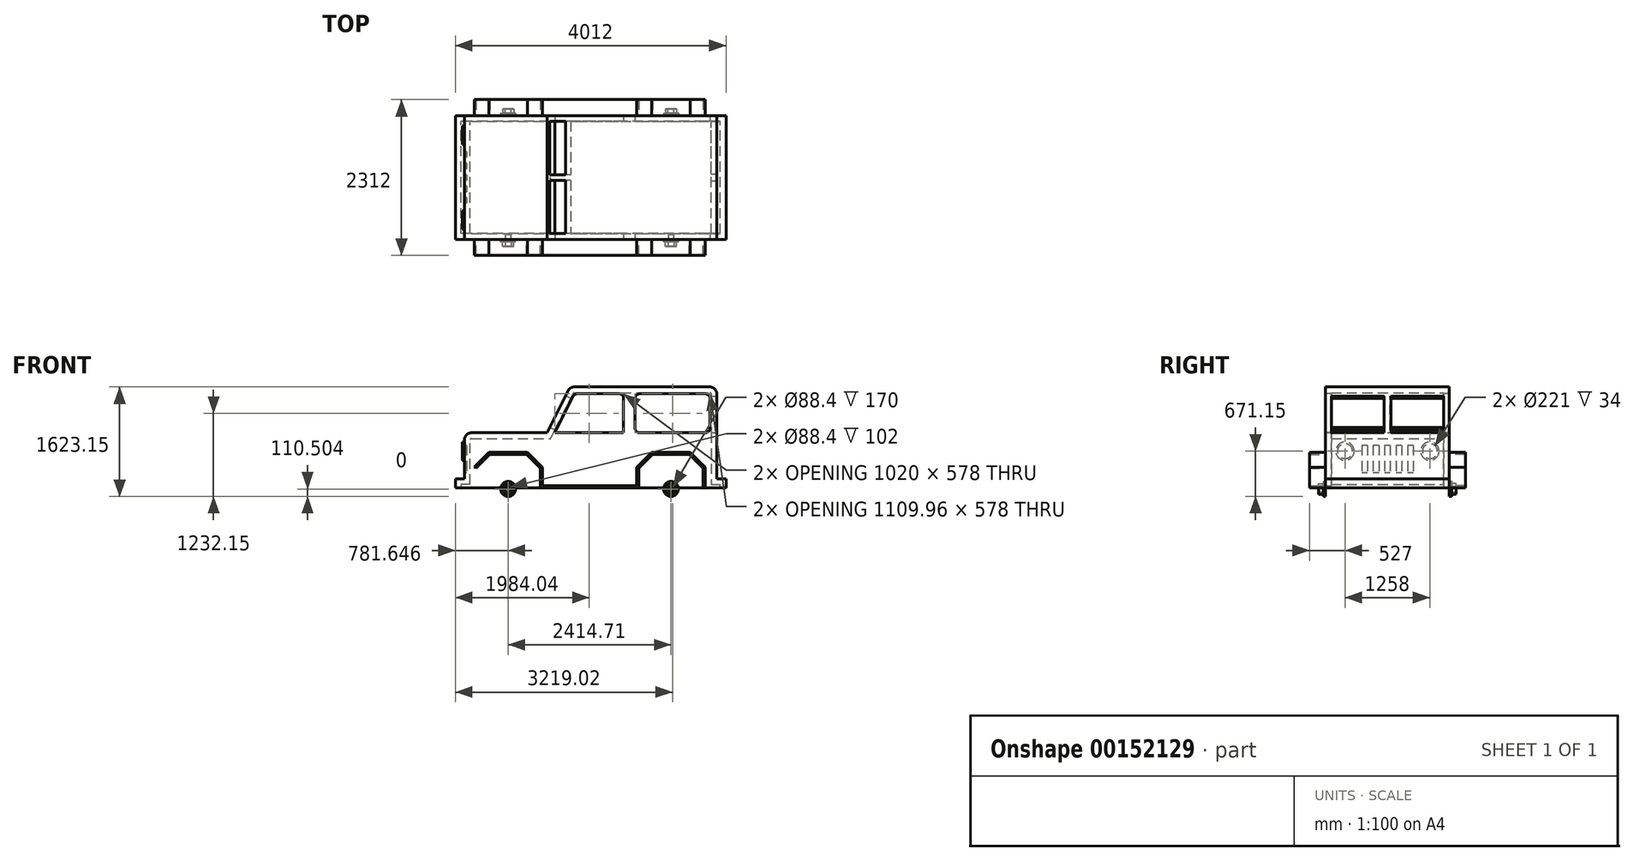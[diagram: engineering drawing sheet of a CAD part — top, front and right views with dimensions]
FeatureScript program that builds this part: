
annotation { "Feature Type Name" : "Feature", "Feature Type Description" : "" }
export const myFeature = defineFeature(function(context is Context, id is Id, definition is map)
    precondition{}
    {
        {
            var Q0;
            Q0=qCreatedBy(makeId("Front.planeOp"),FACE);
            var sketch = newSketch(context, id + "F0", { "sketchPlane" : qUnion([Q0])});
            skLineSegment(sketch, "E0", {"start": v(-54, 4) * mm, "end": v(-54, 21) * mm});
            skLineSegment(sketch, "E1", {"start": v(-51, 24) * mm, "end": v(-18, 24) * mm});
            skLineSegment(sketch, "E2", {"start": v(-18, 24) * mm, "end": v(-8.83, 42.34) * mm});
            skLineSegment(sketch, "E3", {"start": v(-6.15, 44) * mm, "end": v(53, 44) * mm});
            skLineSegment(sketch, "E4", {"start": v(56, 41) * mm, "end": v(56, 4) * mm});
            skLineSegment(sketch, "E5", {"start": v(56, 0) * mm, "end": v(-54, 0) * mm});
            skLineSegment(sketch, "E6", {"start": v(-36, 0) * mm, "end": v(36, 0) * mm, "construction": true});
            skCircle(sketch, "E7", {"center": v(-36, 0) * mm, "radius": 11.5 * mm, "construction": true});
            skCircle(sketch, "E8", {"center": v(36, 0) * mm, "radius": 11.5 * mm, "construction": true});
            skPoint(sketch, "E9.visualSharp", {"position": v(-54, 24) * mm});
            skArc(sketch, "E9.filletArc", {"start": v(-51, 24) * mm, "mid": v(-53.12, 23.12) * mm, "end": v(-54, 21) * mm});
            skPoint(sketch, "E10.visualSharp", {"position": v(-8, 44) * mm});
            skArc(sketch, "E10.filletArc", {"start": v(-6.15, 44) * mm, "mid": v(-7.72, 43.55) * mm, "end": v(-8.83, 42.34) * mm});
            skPoint(sketch, "E11.visualSharp", {"position": v(56, 44) * mm});
            skArc(sketch, "E11.filletArc", {"start": v(56, 41) * mm, "mid": v(55.12, 43.12) * mm, "end": v(53, 44) * mm});
            skPoint(sketch, "E12.visualSharp", {"position": v(56, 0) * mm});
            skLineSegment(sketch, "E13.bottom", {"start": v(-54, 4) * mm, "end": v(-58, 4) * mm});
            skLineSegment(sketch, "E13.top", {"start": v(-54, 0) * mm, "end": v(-58, 0) * mm});
            skLineSegment(sketch, "E13.right", {"start": v(-58, 4) * mm, "end": v(-58, 0) * mm});
            skLineSegment(sketch, "E14.bottom", {"start": v(56, 0) * mm, "end": v(60, 0) * mm});
            skLineSegment(sketch, "E14.top", {"start": v(56, 4) * mm, "end": v(60, 4) * mm});
            skLineSegment(sketch, "E14.right", {"start": v(60, 0) * mm, "end": v(60, 4) * mm});
            skSolve(sketch);
        }
        {
            var Q0;
            Q0=qSketchRegion(id+"F0",true);
            extrude(context, id + "F1", {"entities" : qUnion([Q0]), "depth" : 27 * mm, "hasSecondDirection" : true, "secondDirectionOppositeDirection" : true, "secondDirectionDepth" : 27 * mm});
        }
        {
            var Q0;
            Q0=makeQuery(id+"F1.opExtrude","SWEPT_FACE",FACE,{"disambiguationData":[OSD([sQuery(id+"F0.wireOp",EDGE,"E5")])]});
            shell(context, id + "F2", {"entities" : qUnion([Q0]), "thickness" : 2.5 * mm});
        }
        {
            var Q0;
            Q0=makeQuery(id+"F1.opExtrude","SWEPT_FACE",FACE,{"disambiguationData":[OSD([sQuery(id+"F0.wireOp",EDGE,"E2")])]});
            var sketch = newSketch(context, id + "F3", { "sketchPlane" : qUnion([Q0])});
            skLineSegment(sketch, "E15.0", {"start": v(-24.5, 31.42) * mm, "end": v(-24.5, 15.92) * mm});
            skLineSegment(sketch, "E15.1", {"start": v(24.5, 31.42) * mm, "end": v(1.25, 31.42) * mm});
            skLineSegment(sketch, "E15.2", {"start": v(24.5, 15.92) * mm, "end": v(24.5, 31.42) * mm});
            skLineSegment(sketch, "E15.3", {"start": v(-24.5, 15.92) * mm, "end": v(-1.25, 15.92) * mm});
            skLineSegment(sketch, "E16.top", {"start": v(-1.25, 15.92) * mm, "end": v(1.25, 15.92) * mm});
            skLineSegment(sketch, "E16.left", {"start": v(-1.25, 31.42) * mm, "end": v(-1.25, 15.92) * mm});
            skLineSegment(sketch, "E16.right", {"start": v(1.25, 31.42) * mm, "end": v(1.25, 15.92) * mm});
            skLineSegment(sketch, "E17.trimOffspring", {"start": v(1.25, 15.92) * mm, "end": v(24.5, 15.92) * mm});
            skLineSegment(sketch, "E18.trimOffspring", {"start": v(-1.25, 31.42) * mm, "end": v(-24.5, 31.42) * mm});
            skSolve(sketch);
        }
        {
            var Q0;
            Q0=qSketchRegion(id+"F3",true);
            extrude(context, id + "F4", {"entities" : qUnion([Q0]), "operationType" : NewBodyOperationType.REMOVE, "endBound" : BoundingType.UP_TO_NEXT, "oppositeDirection" : true, "depth" : 25 * mm});
        }
        {
            var Q0;
            Q0=makeQuery(id+"F1.opExtrude","CAP_FACE",FACE,{"disambiguationData":[OSD([sQuery(id+"F0.wireOp",EDGE,"E0"),sQuery(id+"F0.wireOp",EDGE,"E1"),sQuery(id+"F0.wireOp",EDGE,"E2"),sQuery(id+"F0.wireOp",EDGE,"E3"),sQuery(id+"F0.wireOp",EDGE,"E4"),sQuery(id+"F0.wireOp",EDGE,"E5"),sQuery(id+"F0.wireOp",EDGE,"E9.filletArc"),sQuery(id+"F0.wireOp",EDGE,"E10.filletArc"),sQuery(id+"F0.wireOp",EDGE,"E11.filletArc"),sQuery(id+"F0.wireOp",EDGE,"E13.bottom"),sQuery(id+"F0.wireOp",EDGE,"E13.top"),sQuery(id+"F0.wireOp",EDGE,"E13.right"),sQuery(id+"F0.wireOp",EDGE,"E14.bottom"),sQuery(id+"F0.wireOp",EDGE,"E14.top"),sQuery(id+"F0.wireOp",EDGE,"E14.right")])],"isStart":false});
            var sketch = newSketch(context, id + "F5", { "sketchPlane" : qUnion([Q0])});
            skLineSegment(sketch, "E19", {"start": v(-14.65, 24) * mm, "end": v(-6.7, 39.9) * mm});
            skLineSegment(sketch, "E20", {"start": v(-4.9, 41) * mm, "end": v(13.35, 41) * mm});
            skLineSegment(sketch, "E21", {"start": v(15.35, 39) * mm, "end": v(15.35, 24) * mm});
            skLineSegment(sketch, "E22", {"start": v(15.35, 24) * mm, "end": v(-14.65, 24) * mm});
            skLineSegment(sketch, "E23.bottom", {"start": v(22.35, 41) * mm, "end": v(51, 41) * mm});
            skLineSegment(sketch, "E23.top", {"start": v(22.35, 24) * mm, "end": v(51, 24) * mm});
            skLineSegment(sketch, "E23.left", {"start": v(20.35, 39) * mm, "end": v(20.35, 26) * mm});
            skLineSegment(sketch, "E23.right", {"start": v(53, 39) * mm, "end": v(53, 26) * mm});
            skPoint(sketch, "E24.visualSharp", {"position": v(-6.15, 41) * mm});
            skArc(sketch, "E24.filletArc", {"start": v(-4.9, 41) * mm, "mid": v(-5.96, 40.7) * mm, "end": v(-6.7, 39.9) * mm});
            skPoint(sketch, "E25.visualSharp", {"position": v(20.35, 41) * mm});
            skArc(sketch, "E25.filletArc", {"start": v(22.35, 41) * mm, "mid": v(20.94, 40.41) * mm, "end": v(20.35, 39) * mm});
            skPoint(sketch, "E26.visualSharp", {"position": v(53, 41) * mm});
            skArc(sketch, "E26.filletArc", {"start": v(53, 39) * mm, "mid": v(52.41, 40.41) * mm, "end": v(51, 41) * mm});
            skPoint(sketch, "E27.visualSharp", {"position": v(53, 24) * mm});
            skArc(sketch, "E27.filletArc", {"start": v(51, 24) * mm, "mid": v(52.41, 24.59) * mm, "end": v(53, 26) * mm});
            skPoint(sketch, "E28.visualSharp", {"position": v(20.35, 24) * mm});
            skArc(sketch, "E28.filletArc", {"start": v(20.35, 26) * mm, "mid": v(20.94, 24.59) * mm, "end": v(22.35, 24) * mm});
            skPoint(sketch, "E29.visualSharp", {"position": v(15.35, 41) * mm});
            skArc(sketch, "E29.filletArc", {"start": v(15.35, 39) * mm, "mid": v(14.77, 40.41) * mm, "end": v(13.35, 41) * mm});
            skSolve(sketch);
        }
        {
            var Q0;
            Q0=qSketchRegion(id+"F5",true);
            extrude(context, id + "F6", {"entities" : qUnion([Q0]), "operationType" : NewBodyOperationType.REMOVE, "endBound" : BoundingType.THROUGH_ALL, "oppositeDirection" : true, "depth" : 25 * mm});
        }
        {
            var Q0;
            Q0=makeQuery(id+"F1.opExtrude","SWEPT_FACE",FACE,{"disambiguationData":[OSD([sQuery(id+"F0.wireOp",EDGE,"E4")])]});
            var sketch = newSketch(context, id + "F7", { "sketchPlane" : qUnion([Q0])});
            skLineSegment(sketch, "E30.bottom", {"start": v(24.5, 24) * mm, "end": v(1.5, 24) * mm});
            skLineSegment(sketch, "E30.top", {"start": v(24.5, 40) * mm, "end": v(1.5, 40) * mm});
            skLineSegment(sketch, "E30.left", {"start": v(24.5, 24) * mm, "end": v(24.5, 40) * mm});
            skLineSegment(sketch, "E30.right", {"start": v(1.5, 24) * mm, "end": v(1.5, 40) * mm});
            skLineSegment(sketch, "E31.bottom", {"start": v(-1.5, 24) * mm, "end": v(-24.5, 24) * mm});
            skLineSegment(sketch, "E31.top", {"start": v(-1.5, 40) * mm, "end": v(-24.5, 40) * mm});
            skLineSegment(sketch, "E31.left", {"start": v(-1.5, 24) * mm, "end": v(-1.5, 40) * mm});
            skLineSegment(sketch, "E31.right", {"start": v(-24.5, 24) * mm, "end": v(-24.5, 40) * mm});
            skSolve(sketch);
        }
        {
            var Q0;
            Q0=makeQuery(id+"F1.opExtrude","SWEPT_FACE",FACE,{"disambiguationData":[OSD([sQuery(id+"F0.wireOp",EDGE,"E0")])]});
            var sketch = newSketch(context, id + "F8", { "sketchPlane" : qUnion([Q0])});
            skCircle(sketch, "E32", {"center": v(-18.5, 16) * mm, "radius": 4 * mm});
            skCircle(sketch, "E33", {"center": v(18.5, 16) * mm, "radius": 4 * mm});
            skCircle(sketch, "E34", {"center": v(-18.5, 16) * mm, "radius": 3.25 * mm});
            skCircle(sketch, "E35", {"center": v(18.5, 16) * mm, "radius": 3.25 * mm});
            skSolve(sketch);
        }
        {
            var Q0;
            Q0=qSketchRegion(id+"F7",true);
            extrude(context, id + "F9", {"entities" : qUnion([Q0]), "operationType" : NewBodyOperationType.REMOVE, "endBound" : BoundingType.UP_TO_NEXT, "oppositeDirection" : true, "depth" : 25 * mm});
        }
        {
            var Q0;
            Q0=qSketchRegion(id+"F8",true);
            extrude(context, id + "F10", {"entities" : qUnion([Q0]), "operationType" : NewBodyOperationType.ADD, "depth" : 1 * mm});
        }
        {
            var Q0;
            Q0=makeQuery(id+"F1.opExtrude","CAP_FACE",FACE,{"disambiguationData":[OSD([sQuery(id+"F0.wireOp",EDGE,"E0"),sQuery(id+"F0.wireOp",EDGE,"E1"),sQuery(id+"F0.wireOp",EDGE,"E2"),sQuery(id+"F0.wireOp",EDGE,"E3"),sQuery(id+"F0.wireOp",EDGE,"E4"),sQuery(id+"F0.wireOp",EDGE,"E5"),sQuery(id+"F0.wireOp",EDGE,"E9.filletArc"),sQuery(id+"F0.wireOp",EDGE,"E10.filletArc"),sQuery(id+"F0.wireOp",EDGE,"E11.filletArc"),sQuery(id+"F0.wireOp",EDGE,"E13.bottom"),sQuery(id+"F0.wireOp",EDGE,"E13.top"),sQuery(id+"F0.wireOp",EDGE,"E13.right"),sQuery(id+"F0.wireOp",EDGE,"E14.bottom"),sQuery(id+"F0.wireOp",EDGE,"E14.top"),sQuery(id+"F0.wireOp",EDGE,"E14.right")])],"isStart":false});
            var sketch = newSketch(context, id + "F11", { "sketchPlane" : qUnion([Q0])});
            skLineSegment(sketch, "E36", {"start": v(-49.02, 8.5) * mm, "end": v(-43.01, 14.51) * mm});
            skLineSegment(sketch, "E37", {"start": v(-43.01, 14.51) * mm, "end": v(-27.01, 14.51) * mm});
            skLineSegment(sketch, "E38", {"start": v(-27.01, 14.51) * mm, "end": v(-21, 8.5) * mm});
            skLineSegment(sketch, "E39", {"start": v(-21, 8.5) * mm, "end": v(-21, 0) * mm});
            skLineSegment(sketch, "E40", {"start": v(-21, 0) * mm, "end": v(22, 0) * mm});
            skLineSegment(sketch, "E41", {"start": v(22, 0) * mm, "end": v(22, 8.5) * mm});
            skLineSegment(sketch, "E42", {"start": v(22, 8.5) * mm, "end": v(28.01, 14.51) * mm});
            skLineSegment(sketch, "E43", {"start": v(28.01, 14.51) * mm, "end": v(44.01, 14.51) * mm});
            skLineSegment(sketch, "E44", {"start": v(44.01, 14.51) * mm, "end": v(50.02, 8.5) * mm});
            skLineSegment(sketch, "E45", {"start": v(50.02, 8.5) * mm, "end": v(50.02, 0) * mm});
            skLineSegment(sketch, "E46.0", {"start": v(51.02, 8.91) * mm, "end": v(51.02, 0) * mm});
            skLineSegment(sketch, "E46.1", {"start": v(44.42, 15.51) * mm, "end": v(51.02, 8.91) * mm});
            skLineSegment(sketch, "E46.2", {"start": v(27.6, 15.51) * mm, "end": v(44.42, 15.51) * mm});
            skLineSegment(sketch, "E46.3", {"start": v(21, 8.91) * mm, "end": v(27.6, 15.51) * mm});
            skLineSegment(sketch, "E46.4", {"start": v(21, 1) * mm, "end": v(21, 8.91) * mm});
            skLineSegment(sketch, "E46.5", {"start": v(-20, 1) * mm, "end": v(21, 1) * mm});
            skLineSegment(sketch, "E46.6", {"start": v(-20, 8.91) * mm, "end": v(-20, 1) * mm});
            skLineSegment(sketch, "E46.7", {"start": v(-26.6, 15.51) * mm, "end": v(-20, 8.91) * mm});
            skLineSegment(sketch, "E46.8", {"start": v(-43.42, 15.51) * mm, "end": v(-26.6, 15.51) * mm});
            skLineSegment(sketch, "E46.9", {"start": v(-49.73, 9.2) * mm, "end": v(-43.42, 15.51) * mm});
            skLineSegment(sketch, "E47", {"start": v(-49.73, 9.2) * mm, "end": v(-49.02, 8.5) * mm});
            skLineSegment(sketch, "E48", {"start": v(50.02, 0) * mm, "end": v(51.02, 0) * mm});
            skSolve(sketch);
        }
        {
            var Q0;
            Q0=qSketchRegion(id+"F11",true);
            var Q1;
            Q1=qConstructionFilter(qBodyType(qCreatedBy(id+"F11",EDGE),BodyType.WIRE),ConstructionObject.NO);
            extrude(context, id + "F12", {"entities" : qUnion([Q0]), "surfaceEntities" : qUnion([Q1]), "depth" : 7 * mm});
        }
        {
            var Q0;
            Q0=makeQuery(id+"F12.opExtrude","SWEPT_BODY",BODY,{"disambiguationData":[OSD([sQuery(id+"F11.wireOp",EDGE,"E36"),sQuery(id+"F11.wireOp",EDGE,"E37"),sQuery(id+"F11.wireOp",EDGE,"E38"),sQuery(id+"F11.wireOp",EDGE,"E39"),sQuery(id+"F11.wireOp",EDGE,"E40"),sQuery(id+"F11.wireOp",EDGE,"E41"),sQuery(id+"F11.wireOp",EDGE,"E42"),sQuery(id+"F11.wireOp",EDGE,"E43"),sQuery(id+"F11.wireOp",EDGE,"E44"),sQuery(id+"F11.wireOp",EDGE,"E45"),sQuery(id+"F11.wireOp",EDGE,"E46.0"),sQuery(id+"F11.wireOp",EDGE,"E46.1"),sQuery(id+"F11.wireOp",EDGE,"E46.2"),sQuery(id+"F11.wireOp",EDGE,"E46.3"),sQuery(id+"F11.wireOp",EDGE,"E46.4"),sQuery(id+"F11.wireOp",EDGE,"E46.5"),sQuery(id+"F11.wireOp",EDGE,"E46.6"),sQuery(id+"F11.wireOp",EDGE,"E46.7"),sQuery(id+"F11.wireOp",EDGE,"E46.8"),sQuery(id+"F11.wireOp",EDGE,"E46.9"),sQuery(id+"F11.wireOp",EDGE,"E47"),sQuery(id+"F11.wireOp",EDGE,"E48")])]});
            var Q1;
            Q1=qCreatedBy(makeId("Front.planeOp"),FACE);
            mirror(context, id + "F13", {"operationType" : NewBodyOperationType.ADD, "entities" : qUnion([Q0]), "mirrorPlane" : qUnion([Q1])});
        }
        {
            var Q0;
            {var subQ0=sQuery(id+"F0.wireOp",EDGE,"E0");var subQ1=sQuery(id+"F0.wireOp",EDGE,"E1");var subQ2=sQuery(id+"F0.wireOp",EDGE,"E2");var subQ3=sQuery(id+"F0.wireOp",EDGE,"E3");var subQ4=sQuery(id+"F0.wireOp",EDGE,"E4");var subQ5=sQuery(id+"F0.wireOp",EDGE,"E5");var subQ6=sQuery(id+"F0.wireOp",EDGE,"E9.filletArc");var subQ7=sQuery(id+"F0.wireOp",EDGE,"E10.filletArc");var subQ8=sQuery(id+"F0.wireOp",EDGE,"E11.filletArc");var subQ9=sQuery(id+"F0.wireOp",EDGE,"E13.bottom");var subQ10=sQuery(id+"F0.wireOp",EDGE,"E13.top");var subQ11=sQuery(id+"F0.wireOp",EDGE,"E13.right");var subQ12=sQuery(id+"F0.wireOp",EDGE,"E14.bottom");var subQ13=sQuery(id+"F0.wireOp",EDGE,"E14.top");var subQ14=sQuery(id+"F0.wireOp",EDGE,"E14.right");Q0=makeQuery(id+"F13.boolean.opBoolean","SPLIT",FACE,{"disambiguationData":[TD([makeQuery(id+"F1.opExtrude","SWEPT_FACE",FACE,{"disambiguationData":[OSD([subQ0])]})])],"derivedFrom":makeQuery(id+"F1.opExtrude","CAP_FACE",FACE,{"disambiguationData":[OSD([subQ0,subQ1,subQ2,subQ3,subQ4,subQ5,subQ6,subQ7,subQ8,subQ9,subQ10,subQ11,subQ12,subQ13,subQ14])],"isStart":false})});}
            var sketch = newSketch(context, id + "F14", { "sketchPlane" : qUnion([Q0])});
            skCircle(sketch, "E49", {"center": v(-35.01, -0.49) * mm, "radius": 3.25 * mm});
            skCircle(sketch, "E50", {"center": v(36.01, -0.49) * mm, "radius": 3.25 * mm});
            skLineSegment(sketch, "E51", {"start": v(-35.01, -0.49) * mm, "end": v(-35.01, 14.51) * mm, "construction": true});
            skLineSegment(sketch, "E52", {"start": v(36.01, -0.49) * mm, "end": v(36.01, 14.51) * mm, "construction": true});
            skSolve(sketch);
        }
        {
            var Q0;
            Q0=qSketchRegion(id+"F14",true);
            extrude(context, id + "F15", {"entities" : qUnion([Q0]), "depth" : 1 * mm});
        }
        {
            var Q0;
            Q0=makeQuery(id+"F15.opExtrude","CAP_FACE",FACE,{"disambiguationData":[OSD([sQuery(id+"F14.wireOp",EDGE,"E49")])],"isStart":false});
            var sketch = newSketch(context, id + "F16", { "sketchPlane" : qUnion([Q0])});
            skCircle(sketch, "E53", {"center": v(-35.01, -0.49) * mm, "radius": 2.4 * mm});
            skCircle(sketch, "E54", {"center": v(36.01, -0.49) * mm, "radius": 2.4 * mm});
            skSolve(sketch);
        }
        {
            var Q0;
            Q0=qSketchRegion(id+"F16",true);
            extrude(context, id + "F17", {"entities" : qUnion([Q0]), "operationType" : NewBodyOperationType.ADD, "depth" : 2 * mm});
        }
        {
            var Q0;
            Q0=makeQuery(id+"F17.opExtrude","CAP_FACE",FACE,{"disambiguationData":[OSD([sQuery(id+"F16.wireOp",EDGE,"E53")])],"isStart":false});
            var sketch = newSketch(context, id + "F18", { "sketchPlane" : qUnion([Q0])});
            skCircle(sketch, "E55", {"center": v(-35.01, -0.49) * mm, "radius": 1.3 * mm});
            skCircle(sketch, "E56", {"center": v(36.01, -0.49) * mm, "radius": 1.3 * mm});
            skSolve(sketch);
        }
        {
            var Q0;
            Q0=qSketchRegion(id+"F18",true);
            extrude(context, id + "F19", {"entities" : qUnion([Q0]), "operationType" : NewBodyOperationType.REMOVE, "oppositeDirection" : true, "depth" : 5 * mm});
        }
        {
            var Q0;
            Q0=makeQuery(id+"F15.opExtrude","SWEPT_BODY",BODY,{"disambiguationData":[OSD([sQuery(id+"F14.wireOp",EDGE,"E50")])]});
            var Q1;
            Q1=makeQuery(id+"F15.opExtrude","SWEPT_BODY",BODY,{"disambiguationData":[OSD([sQuery(id+"F14.wireOp",EDGE,"E49")])]});
            var Q2;
            Q2=qCreatedBy(makeId("Front.planeOp"),FACE);
            mirror(context, id + "F20", {"operationType" : NewBodyOperationType.ADD, "entities" : qUnion([Q0, Q1]), "mirrorPlane" : qUnion([Q2])});
        }
        {
            var Q0;
            {var subQ0=sQuery(id+"F0.wireOp",EDGE,"E0");var subQ2=sQuery(id+"F0.wireOp",EDGE,"E9.filletArc");Q0=makeQuery(id+"F10.boolean.opBoolean","SPLIT",FACE,{"disambiguationData":[TD([makeQuery(id+"F1.opExtrude","SWEPT_FACE",FACE,{"disambiguationData":[OSD([subQ2])]})])],"derivedFrom":makeQuery(id+"F1.opExtrude","SWEPT_FACE",FACE,{"disambiguationData":[OSD([subQ0])]})});}
            var sketch = newSketch(context, id + "F21", { "sketchPlane" : qUnion([Q0])});
            skLineSegment(sketch, "E57.bottom", {"start": v(-11.25, 18.5) * mm, "end": v(-8.75, 18.5) * mm});
            skLineSegment(sketch, "E57.top", {"start": v(-11.25, 6.5) * mm, "end": v(-8.75, 6.5) * mm});
            skLineSegment(sketch, "E57.left", {"start": v(-11.25, 18.5) * mm, "end": v(-11.25, 6.5) * mm});
            skLineSegment(sketch, "E57.right", {"start": v(-8.75, 18.5) * mm, "end": v(-8.75, 6.5) * mm});
            skLineSegment(sketch, "E58.bottom", {"start": v(-6.25, 18.5) * mm, "end": v(-3.75, 18.5) * mm});
            skLineSegment(sketch, "E58.top", {"start": v(-6.25, 6.5) * mm, "end": v(-3.75, 6.5) * mm});
            skLineSegment(sketch, "E58.left", {"start": v(-6.25, 18.5) * mm, "end": v(-6.25, 6.5) * mm});
            skLineSegment(sketch, "E58.right", {"start": v(-3.75, 18.5) * mm, "end": v(-3.75, 6.5) * mm});
            skLineSegment(sketch, "E59.bottom", {"start": v(3.75, 18.5) * mm, "end": v(6.25, 18.5) * mm});
            skLineSegment(sketch, "E59.top", {"start": v(3.75, 6.5) * mm, "end": v(6.25, 6.5) * mm});
            skLineSegment(sketch, "E59.left", {"start": v(3.75, 18.5) * mm, "end": v(3.75, 6.5) * mm});
            skLineSegment(sketch, "E59.right", {"start": v(6.25, 18.5) * mm, "end": v(6.25, 6.5) * mm});
            skLineSegment(sketch, "E60.bottom", {"start": v(8.75, 18.5) * mm, "end": v(11.25, 18.5) * mm});
            skLineSegment(sketch, "E60.top", {"start": v(8.75, 6.5) * mm, "end": v(11.25, 6.5) * mm});
            skLineSegment(sketch, "E60.left", {"start": v(8.75, 18.5) * mm, "end": v(8.75, 6.5) * mm});
            skLineSegment(sketch, "E60.right", {"start": v(11.25, 18.5) * mm, "end": v(11.25, 6.5) * mm});
            skLineSegment(sketch, "E61.left", {"start": v(-1.25, 18.5) * mm, "end": v(-1.25, 6.5) * mm});
            skLineSegment(sketch, "E61.top", {"start": v(-1.25, 6.5) * mm, "end": v(1.25, 6.5) * mm});
            skLineSegment(sketch, "E61.bottom", {"start": v(-1.25, 18.5) * mm, "end": v(1.25, 18.5) * mm});
            skLineSegment(sketch, "E61.right", {"start": v(1.25, 18.5) * mm, "end": v(1.25, 6.5) * mm});
            skLineSegment(sketch, "E62", {"start": v(-8.75, 6.5) * mm, "end": v(-6.25, 6.5) * mm, "construction": true});
            skLineSegment(sketch, "E63", {"start": v(-3.75, 6.5) * mm, "end": v(-1.25, 6.5) * mm, "construction": true});
            skLineSegment(sketch, "E64", {"start": v(1.25, 6.5) * mm, "end": v(3.75, 6.5) * mm, "construction": true});
            skLineSegment(sketch, "E65", {"start": v(6.25, 6.5) * mm, "end": v(8.75, 6.5) * mm, "construction": true});
            skSolve(sketch);
        }
        {
            var Q0;
            Q0=qSketchRegion(id+"F21",true);
            extrude(context, id + "F22", {"entities" : qUnion([Q0]), "operationType" : NewBodyOperationType.REMOVE, "oppositeDirection" : true, "depth" : 1 * mm});
        }
        {
            var Q0;
            Q0=makeQuery(id+"F1.opExtrude","SWEPT_BODY",BODY,{"disambiguationData":[OSD([sQuery(id+"F0.wireOp",EDGE,"E0"),sQuery(id+"F0.wireOp",EDGE,"E1"),sQuery(id+"F0.wireOp",EDGE,"E2"),sQuery(id+"F0.wireOp",EDGE,"E3"),sQuery(id+"F0.wireOp",EDGE,"E4"),sQuery(id+"F0.wireOp",EDGE,"E5"),sQuery(id+"F0.wireOp",EDGE,"E9.filletArc"),sQuery(id+"F0.wireOp",EDGE,"E10.filletArc"),sQuery(id+"F0.wireOp",EDGE,"E11.filletArc"),sQuery(id+"F0.wireOp",EDGE,"E13.bottom"),sQuery(id+"F0.wireOp",EDGE,"E13.top"),sQuery(id+"F0.wireOp",EDGE,"E13.right"),sQuery(id+"F0.wireOp",EDGE,"E14.bottom"),sQuery(id+"F0.wireOp",EDGE,"E14.top"),sQuery(id+"F0.wireOp",EDGE,"E14.right")])]});
            var Q1;
            Q1=qCreatedBy(makeId("Origin.pointOp"),VERTEX);
            transform(context, id + "F23", {"entities" : qUnion([Q0]), "transformType" : TransformType.SCALE_UNIFORMLY, "scale" : 34, "scalePoint" : qUnion([Q1]), "makeCopy" : false});
        }
    });
